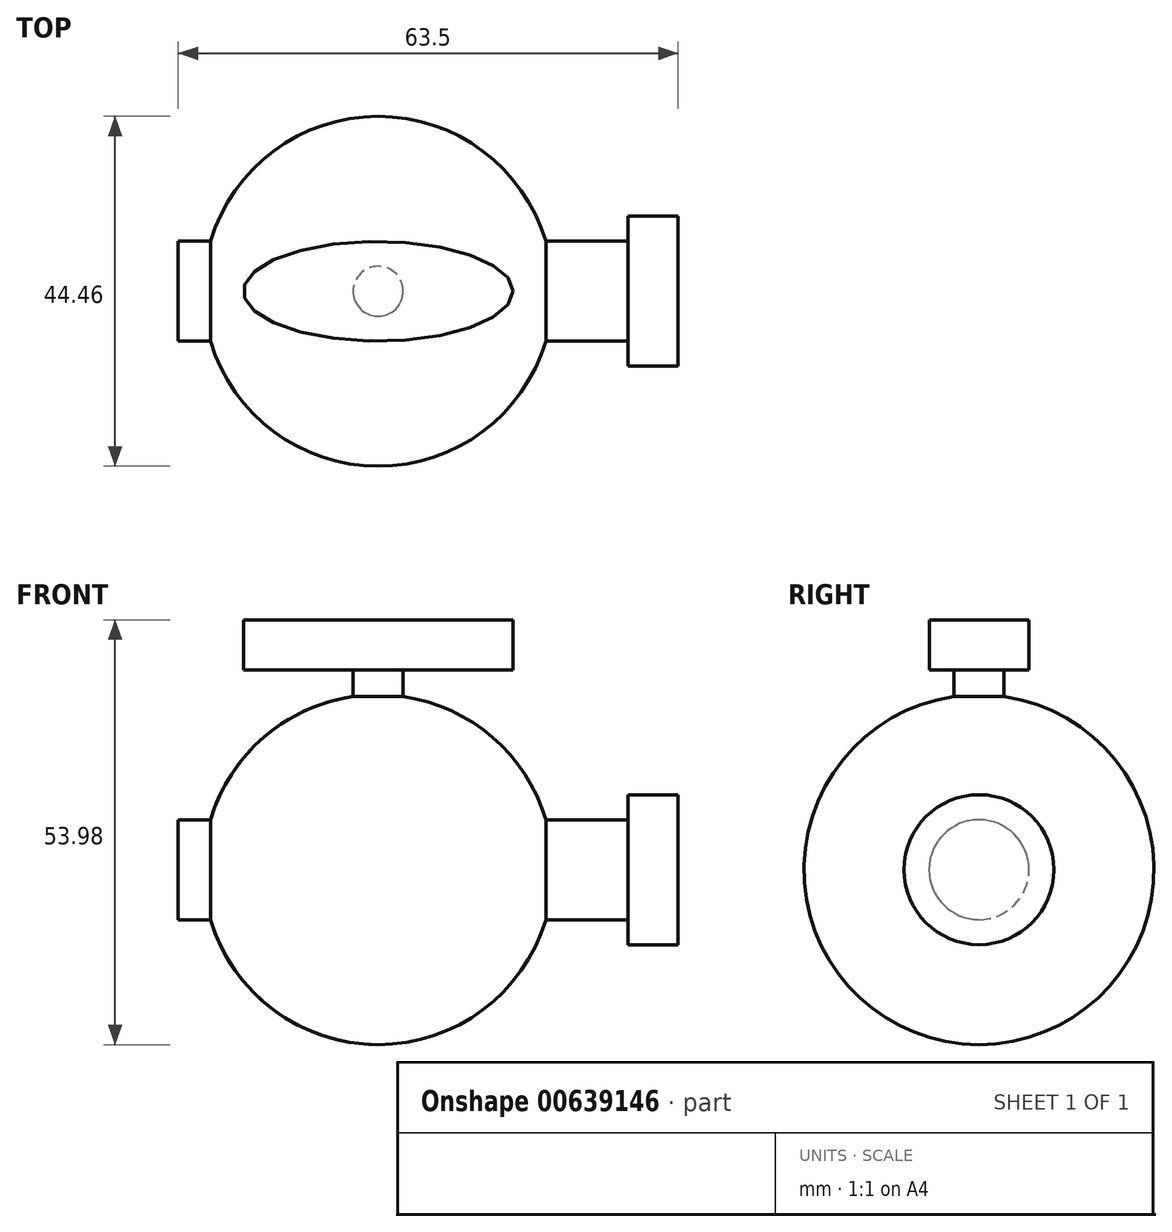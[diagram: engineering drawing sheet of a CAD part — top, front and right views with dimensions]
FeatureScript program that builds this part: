
annotation { "Feature Type Name" : "Feature", "Feature Type Description" : "" }
export const myFeature = defineFeature(function(context is Context, id is Id, definition is map)
    precondition{}
    {
        {
            var Q0;
            Q0=qCreatedBy(makeId("Front.planeOp"),FACE);
            var sketch = newSketch(context, id + "F0", { "sketchPlane" : qUnion([Q0])});
            skCircle(sketch, "E0", {"center": v(0, 0) * mm, "radius": 22.23 * mm});
            skLineSegment(sketch, "E1", {"start": v(0, -45.14) * mm, "end": v(0, 40.49) * mm});
            skSolve(sketch);
        }
        {
            var Q0;
            {var subQ0=sQuery(id+"F0.wireOp",EDGE,"E1");var subQ1=sQuery(id+"F0.wireOp",EDGE,"E0");var subQ2=makeQuery(id+"F0.imprint","INTERSECT",VERTEX,{"disambiguationData":[OD(0.0)],"derivedFrom":[subQ1,subQ0]});Q0=makeQuery(id+"F0.imprint","IMPRINT",FACE,{"disambiguationData":[TD([[makeQuery(id+"F0.imprint","IMPRINT",EDGE,{"disambiguationData":[TD([[subQ2,1.0]])],"derivedFrom":subQ1}),1.0]])]});}
            var Q1;
            Q1=sQuery(id+"F0.wireOp",EDGE,"E1");
            revolve(context, id + "F1", {"entities" : qUnion([Q0]), "axis" : qUnion([Q1]), "revolveType" : RevolveType.FULL});
        }
        {
            var Q0;
            Q0=qCreatedBy(makeId("Top.planeOp"),FACE);
            var sketch = newSketch(context, id + "F2", { "sketchPlane" : qUnion([Q0])});
            skEllipse(sketch, "E2", {"center": v(0, 0) * mm, "majorRadius": 17.1 * mm, "minorRadius": 6.33 * mm, "majorAxis": v(1, 0)});
            skSolve(sketch);
        }
        {
            var Q0;
            Q0=makeQuery(id+"F2.imprint","IMPRINT",FACE,{"disambiguationData":[TD([[makeQuery(id+"F2.imprint","IMPRINT",EDGE,{"derivedFrom":sQuery(id+"F2.wireOp",EDGE,"E2")}),1.0]])]});
            extrude(context, id + "F3", {"entities" : qUnion([Q0]), "depth" : 31.75 * mm, "offsetDistance" : 25.4 * mm, "hasSecondDirection" : true, "secondDirectionOppositeDirection" : false, "secondDirectionDepth" : 25.4 * mm});
        }
        {
            var Q0;
            Q0=qCreatedBy(makeId("Right.planeOp"),FACE);
            var sketch = newSketch(context, id + "F4", { "sketchPlane" : qUnion([Q0])});
            skCircle(sketch, "E3", {"center": v(0, 0) * mm, "radius": 6.35 * mm});
            skCircle(sketch, "E4.0", {"center": v(0, 0) * mm, "radius": 9.53 * mm});
            skSolve(sketch);
        }
        {
            var Q0;
            Q0=makeQuery(id+"F4.imprint","IMPRINT",FACE,{"disambiguationData":[TD([[makeQuery(id+"F4.imprint","IMPRINT",EDGE,{"derivedFrom":sQuery(id+"F4.wireOp",EDGE,"E3")}),1.0]])]});
            extrude(context, id + "F5", {"entities" : qUnion([Q0]), "depth" : 38.1 * mm, "offsetDistance" : 25.4 * mm, "hasSecondDirection" : true, "secondDirectionOppositeDirection" : true, "secondDirectionDepth" : 25.4 * mm});
        }
        {
            var Q0;
            Q0=qSketchRegion(id+"F4",true);
            extrude(context, id + "F6", {"entities" : qUnion([Q0]), "operationType" : NewBodyOperationType.ADD, "depth" : 38.1 * mm, "offsetDistance" : 25.4 * mm, "hasSecondDirection" : true, "secondDirectionOppositeDirection" : false, "secondDirectionDepth" : 31.75 * mm});
        }
        {
            var Q0;
            Q0=makeQuery(id+"F3.opExtrude","CAP_FACE",FACE,{"disambiguationData":[OSD([sQuery(id+"F2.wireOp",EDGE,"E2")])],"isStart":false});
            var sketch = newSketch(context, id + "F7", { "sketchPlane" : qUnion([Q0])});
            skCircle(sketch, "E5", {"center": v(0, 0) * mm, "radius": 3.18 * mm});
            skSolve(sketch);
        }
        {
            var Q0;
            Q0=qSketchRegion(id+"F7",true);
            extrude(context, id + "F8", {"entities" : qUnion([Q0]), "operationType" : NewBodyOperationType.ADD, "oppositeDirection" : true, "depth" : 25.4 * mm, "offsetDistance" : 25.4 * mm});
        }
    });
